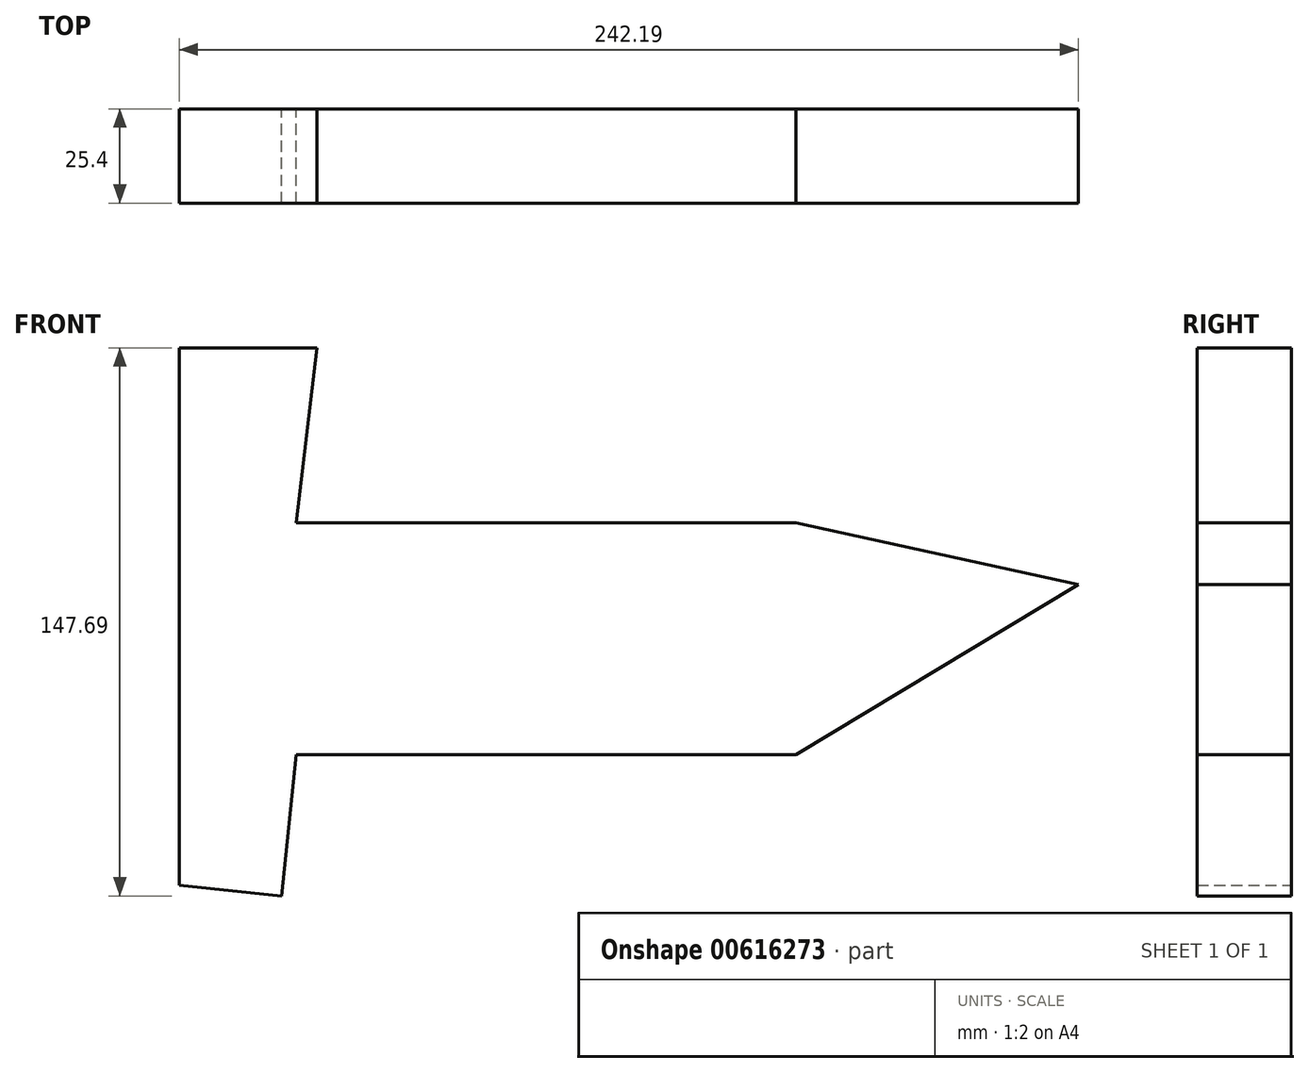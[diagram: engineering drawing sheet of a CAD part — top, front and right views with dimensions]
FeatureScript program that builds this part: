
annotation { "Feature Type Name" : "Feature", "Feature Type Description" : "" }
export const myFeature = defineFeature(function(context is Context, id is Id, definition is map)
    precondition{}
    {
        {
            var Q0;
            Q0=qCreatedBy(makeId("Front.planeOp"),FACE);
            var sketch = newSketch(context, id + "F0", { "sketchPlane" : qUnion([Q0])});
            skLineSegment(sketch, "E0.bottom", {"start": v(-152.37, -45.74) * mm, "end": v(13.76, -45.74) * mm});
            skLineSegment(sketch, "E0.top", {"start": v(-152.37, 16.73) * mm, "end": v(13.76, 16.73) * mm});
            skLineSegment(sketch, "E0.left", {"start": v(-152.37, -45.74) * mm, "end": v(-152.37, 16.73) * mm});
            skLineSegment(sketch, "E0.right", {"start": v(13.76, -45.74) * mm, "end": v(13.76, 16.73) * mm});
            skLineSegment(sketch, "E1", {"start": v(13.76, 16.73) * mm, "end": v(89.82, 0) * mm});
            skLineSegment(sketch, "E2", {"start": v(89.82, 0) * mm, "end": v(13.76, -45.74) * mm});
            skLineSegment(sketch, "E3", {"start": v(-152.37, 16.73) * mm, "end": v(-152.37, 63.86) * mm});
            skLineSegment(sketch, "E4", {"start": v(-152.37, 63.86) * mm, "end": v(-115.34, 63.86) * mm});
            skLineSegment(sketch, "E5", {"start": v(-115.34, 63.86) * mm, "end": v(-120.84, 16.73) * mm});
            skLineSegment(sketch, "E6", {"start": v(-120.84, 16.73) * mm, "end": v(-120.84, -45.74) * mm});
            skLineSegment(sketch, "E7", {"start": v(-120.84, -45.74) * mm, "end": v(-124.85, -83.83) * mm});
            skLineSegment(sketch, "E8", {"start": v(-124.85, -83.83) * mm, "end": v(-152.37, -80.94) * mm});
            skLineSegment(sketch, "E9", {"start": v(-152.37, -80.94) * mm, "end": v(-152.37, -45.74) * mm});
            skSolve(sketch);
        }
        {
            var Q0;
            Q0 = qSketchRegion(id + "F0", true);
            extrude(context, id + "F1", {"entities" : qUnion([Q0]), "depth" : 25.4 * mm, "offsetDistance" : 25.4 * mm});
        }
    });
